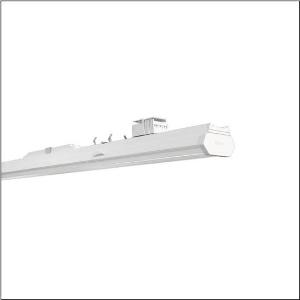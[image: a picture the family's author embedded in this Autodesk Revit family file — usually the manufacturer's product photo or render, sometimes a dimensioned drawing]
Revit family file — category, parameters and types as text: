
# Revit family: licross_r__21_protected_mo_52td11mn4a5g_25e5
name_source: partatom
category: Lighting Fixtures
units: mm (PartAtom-declared; Revit-internal decimal feet)

## family parameters
Cut with Voids When Loaded = No
Host = Face
Light Source = No
Part Type = Normal
Room Calculation Point = No
Round Connector Dimension = Use Diameter
Shared = No

## types (1)
- --- (1 x LED, 10700 lm, 60.5 W, 4000K)
    Apparent Load = 61 VA
    CIE Flux Codes = 83 94 98 100 100
    Color Rendering = 80
    Color Temperature = 4000K
    Default Elevation = 1800 mm
    Description = Licross® 21 Protected MO, luminaire insert, of sheet steel, galvanised, coil coated, white, length: 1.500mm, width: 66mm, height: 67mm, LED rated luminous flux: 10.700lm, light colour: 840, control gear: ON/OFF Multilumen, with plug, 3-pole, with phase selection, mains connection: 220..240V, AC, 50/60Hz, rated input power: 61W, halogen-free wiring, primary light control with lens, of plastic, primary optical cover: cover, of PMMA, light emission: direct distribution, primary light characteristic: symmetric, protection rating (complete): IP54, insulation class (complete): insulation class I (protective earthing), certification: CE, ENEC, VDE, UKCA, protection symbol: D if used in an environment with non-conductive dust loads with corresponding accessories, impact resistance: IK06, permissible ambient temperature for indoor applications: -35..+45°C, corresponds to IFS (International Featured Standards) requirements for safety and quality in the food industry, reducing of maximum allowable ambient temperature of 5°C with ceiling mounting, LABS conformity tested according to VDMA 24364:2018-05, packaging unit: 1 piece
    Height = 92 mm
    Lamp = 1 x LED
    Lamp Light Flux = 10700 lm
    Lamp Power = 60.5 W
    Lamp count = 1
    Length = 1500 mm
    Luminous efficacy = 177 lm/W
    Manufacturer = Siteco
    ModVariant = No
    Model = 52TD11MN4A5G
    Mounting Place = Ceiling
    Mounting Type = Pendant
    Number of Poles = 1
    OnlyDefault = Yes
    Power Factor = 1
    Product Name = Licross® 21 Protected MO
    Product group = luminaire insert
    ProductGroupID = 901
    Protection Class = Protection class I
    Protection Degree = IP 54
    RLX_Detail_Level = 1
    RLX_Emergency_Light_Flux = 0 lm
    RLX_Emergency_Type = 0
    RLX_Emergency_Type_DB = No
    RlxData = <blob elided: 21857 chars, md5=c338d455>
    Socket = socket
    Standby Power = 0 W
    System Light Flux = 10700 lm
    System Power = 61 W
    Type Comments = factory setting: luminous flux: 100 % | (A | C | E) | 140 mA
    Type Image = l_1256148.jpg
    URL = http://relux.com
    VarID = @adj_057363
    Voltage = 0 V
    Weight = 0.00 kg
    Width = 88 mm

## geometry (parser evidence)
native form markers: Blend x4, Sweep x10
no freeform markers — native parametric forms only
